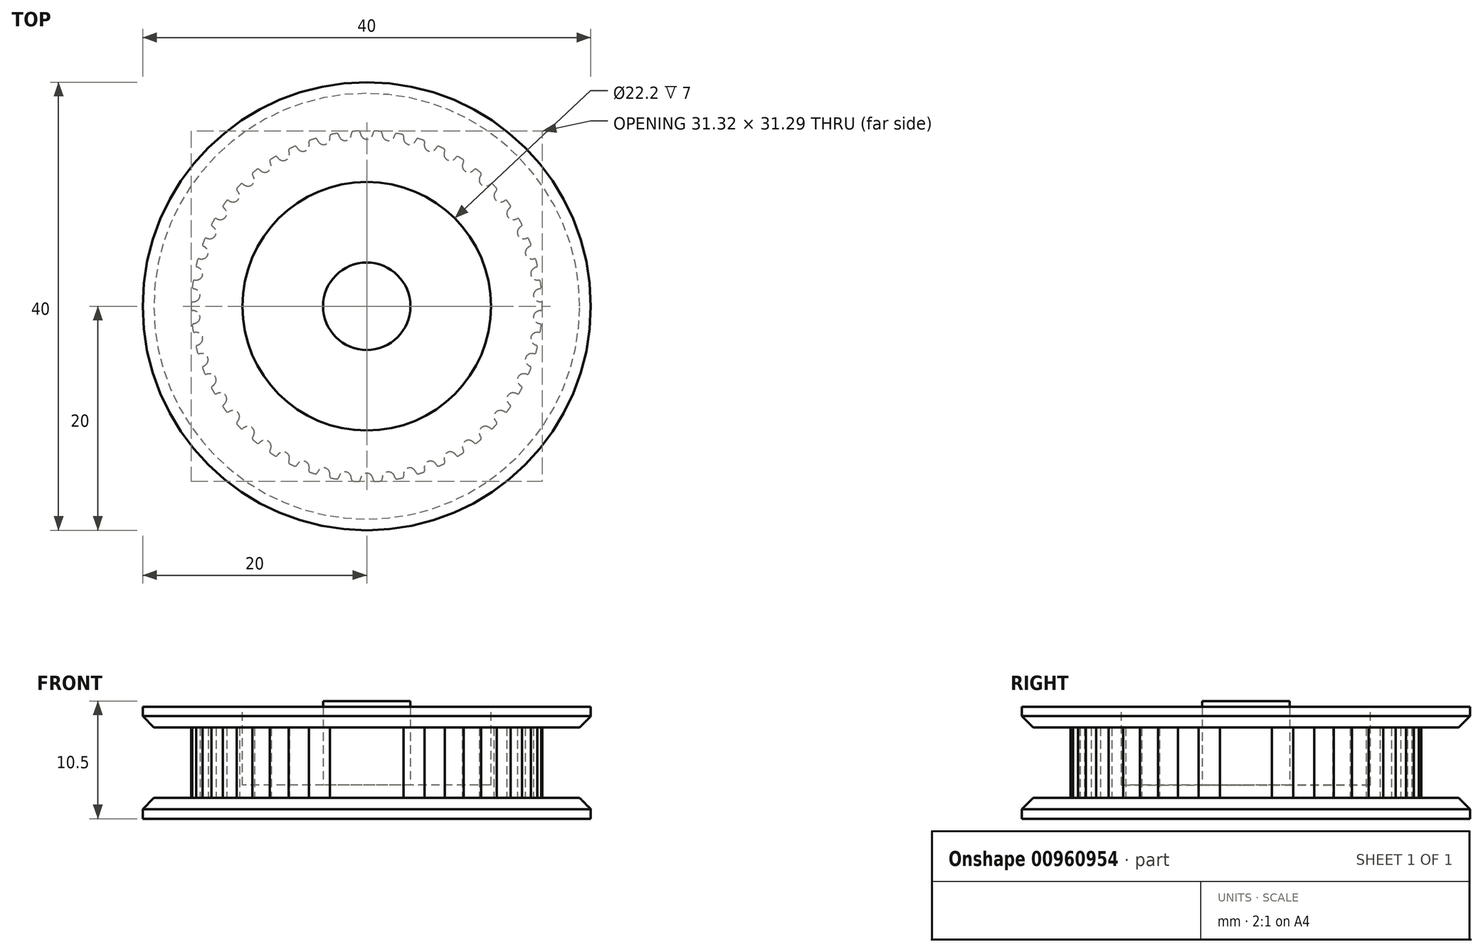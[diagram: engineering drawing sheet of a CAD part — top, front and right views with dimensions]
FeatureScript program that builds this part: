
annotation { "Feature Type Name" : "Feature", "Feature Type Description" : "" }
export const myFeature = defineFeature(function(context is Context, id is Id, definition is map)
    precondition{}
    {
        {
            assignVariable(context, id + "F0", {"variableType" : VariableType.NUMBER, "name" : "TeethP1", "numberValue" : 50});
        }
        {
            assignVariable(context, id + "F1", {"variableType" : VariableType.LENGTH, "name" : "PulleyDepth", "lengthValue" : 10 * mm});
        }
        {
            assignVariable(context, id + "F2", {"variableType" : VariableType.LENGTH, "name" : "BeltWidth", "lengthValue" : 6.3 * mm});
        }
        {
            var Q0;
            Q0=qCreatedBy(makeId("Top.planeOp"),FACE);
            var sketch = newSketch(context, id + "F3", { "sketchPlane" : qUnion([Q0])});
            skPoint(sketch, "E0.center", {"position": v(0, 0) * mm});
            skCircle(sketch, "E1", {"center": v(0, 0) * mm, "radius": 20 * mm});
            skSolve(sketch);
        }
        {
            var Q0;
            Q0 = qSketchRegion(id + "F3", true);
            extrude(context, id + "F4", {"entities" : qUnion([Q0]), "depth" : (getVariable(context, 'PulleyDepth') - getVariable(context, 'BeltWidth')) / 2, "offsetDistance" : 25 * mm});
        }
        {
            var Q0;
            Q0=makeQuery(id+"F4.opExtrude","CAP_FACE",FACE,{"disambiguationData":[OSD([sQuery(id+"F3.wireOp",EDGE,"E1")])],"isStart":false});
            var sketch = newSketch(context, id + "F5", { "sketchPlane" : qUnion([Q0])});
            skCircle(sketch, "E2", {"center": v(0, 0) * mm, "radius": 16.3 * mm, "construction": true});
            skLineSegment(sketch, "E3", {"start": v(0, 0) * mm, "end": v(0, -14.91) * mm});
            skCircle(sketch, "E4", {"center": v(0, 0) * mm, "radius": 14.91 * mm, "construction": true});
            skCircle(sketch, "E5", {"center": v(0, 0) * mm, "radius": 15.66 * mm, "construction": true});
            skCircle(sketch, "E6", {"center": v(0, 0) * mm, "radius": 15.92 * mm, "construction": true});
            skPoint(sketch, "E7", {"position": v(0, -15.92) * mm});
            skArc(sketch, "E8", {"start": v(-0.5, -15.22) * mm, "mid": v(-0.56, -15.37) * mm, "end": v(-0.59, -15.52) * mm});
            skArc(sketch, "E9", {"start": v(0, -14.91) * mm, "mid": v(-0.3, -15) * mm, "end": v(-0.5, -15.22) * mm});
            skArc(sketch, "E10", {"start": v(-0.59, -15.52) * mm, "mid": v(-0.64, -15.6) * mm, "end": v(-0.74, -15.64) * mm});
            skLineSegment(sketch, "E11", {"start": v(0, 0) * mm, "end": v(-0.98, -15.63) * mm, "construction": true});
            skArc(sketch, "E12", {"start": v(-0.74, -15.64) * mm, "mid": v(-0.86, -15.64) * mm, "end": v(-0.98, -15.63) * mm});
            skLineSegment(sketch, "E13.trimOffspring", {"start": v(0, -15.47) * mm, "end": v(0, -16.3) * mm, "construction": true});
            skLineSegment(sketch, "E14.MirrorCS", {"start": v(0, 0) * mm, "end": v(-1.87, -14.8) * mm});
            skArc(sketch, "E15.MirrorCS", {"start": v(-1.87, -14.8) * mm, "mid": v(-1.59, -14.91) * mm, "end": v(-1.41, -15.17) * mm});
            skArc(sketch, "E16.MirrorCS", {"start": v(-1.41, -15.17) * mm, "mid": v(-1.37, -15.31) * mm, "end": v(-1.36, -15.47) * mm});
            skArc(sketch, "E17.MirrorCS", {"start": v(-1.36, -15.47) * mm, "mid": v(-1.32, -15.57) * mm, "end": v(-1.22, -15.61) * mm});
            skArc(sketch, "E18.MirrorCS", {"start": v(-1.22, -15.61) * mm, "mid": v(-1.1, -15.62) * mm, "end": v(-0.98, -15.63) * mm});
            skSolve(sketch);
        }
        {
            var Q0;
            Q0=makeQuery(id+"F5.imprint","IMPRINT",FACE,{"disambiguationData":[TD([[makeQuery(id+"F5.imprint","IMPRINT",EDGE,{"derivedFrom":sQuery(id+"F5.wireOp",EDGE,"E3")}),-1.0]])]});
            extrude(context, id + "F6", {"entities" : qUnion([Q0]), "depth" : getVariable(context, 'BeltWidth'), "offsetDistance" : 25 * mm});
        }
        {
            var Q0;
            Q0=makeQuery(id+"F6.opExtrude","SWEPT_BODY",BODY,{"disambiguationData":[OSD([sQuery(id+"F5.wireOp",EDGE,"E3"),sQuery(id+"F5.wireOp",EDGE,"E8"),sQuery(id+"F5.wireOp",EDGE,"E9"),sQuery(id+"F5.wireOp",EDGE,"E10"),sQuery(id+"F5.wireOp",EDGE,"E12"),sQuery(id+"F5.wireOp",EDGE,"E14.MirrorCS"),sQuery(id+"F5.wireOp",EDGE,"E15.MirrorCS"),sQuery(id+"F5.wireOp",EDGE,"E16.MirrorCS"),sQuery(id+"F5.wireOp",EDGE,"E17.MirrorCS"),sQuery(id+"F5.wireOp",EDGE,"E18.MirrorCS")])]});
            var Q1;
            Q1=makeQuery(id+"F6.opExtrude","SWEPT_EDGE",EDGE,{"disambiguationData":[OSD([sQuery(id+"F5.wireOp",EDGE,"E3"),sQuery(id+"F5.wireOp",EDGE,"E14.MirrorCS")])]});
            circularPattern(context, id + "F7", {"operationType" : NewBodyOperationType.ADD, "entities" : qUnion([Q0]), "axis" : qUnion([Q1]), "angle" : 360 * degree, "instanceCount" : getVariable(context, 'TeethP1'), "equalSpace" : true});
        }
        {
            var Q0;
            Q0=makeQuery(id+"F4.opExtrude","CAP_FACE",FACE,{"disambiguationData":[OSD([sQuery(id+"F3.wireOp",EDGE,"E1")])],"isStart":true});
            var Q1;
            {var subQ0=makeQuery(id+"F6.opExtrude","CAP_FACE",FACE,{"disambiguationData":[OSD([sQuery(id+"F5.wireOp",EDGE,"E3"),sQuery(id+"F5.wireOp",EDGE,"E8"),sQuery(id+"F5.wireOp",EDGE,"E9"),sQuery(id+"F5.wireOp",EDGE,"E10"),sQuery(id+"F5.wireOp",EDGE,"E12"),sQuery(id+"F5.wireOp",EDGE,"E14.MirrorCS"),sQuery(id+"F5.wireOp",EDGE,"E15.MirrorCS"),sQuery(id+"F5.wireOp",EDGE,"E16.MirrorCS"),sQuery(id+"F5.wireOp",EDGE,"E17.MirrorCS"),sQuery(id+"F5.wireOp",EDGE,"E18.MirrorCS")])],"isStart":false});Q1=makeQuery(id+"F7.boolean.opBoolean","MERGE",FACE,{"derivedFrom":[subQ0,makeQuery(id+"F7.opPattern","COPY",FACE,{"derivedFrom":subQ0,"instanceName":"1"}),makeQuery(id+"F7.opPattern","COPY",FACE,{"derivedFrom":subQ0,"instanceName":"2"}),makeQuery(id+"F7.opPattern","COPY",FACE,{"derivedFrom":subQ0,"instanceName":"3"}),makeQuery(id+"F7.opPattern","COPY",FACE,{"derivedFrom":subQ0,"instanceName":"4"}),makeQuery(id+"F7.opPattern","COPY",FACE,{"derivedFrom":subQ0,"instanceName":"5"}),makeQuery(id+"F7.opPattern","COPY",FACE,{"derivedFrom":subQ0,"instanceName":"6"}),makeQuery(id+"F7.opPattern","COPY",FACE,{"derivedFrom":subQ0,"instanceName":"7"}),makeQuery(id+"F7.opPattern","COPY",FACE,{"derivedFrom":subQ0,"instanceName":"8"}),makeQuery(id+"F7.opPattern","COPY",FACE,{"derivedFrom":subQ0,"instanceName":"9"}),makeQuery(id+"F7.opPattern","COPY",FACE,{"derivedFrom":subQ0,"instanceName":"10"}),makeQuery(id+"F7.opPattern","COPY",FACE,{"derivedFrom":subQ0,"instanceName":"11"}),makeQuery(id+"F7.opPattern","COPY",FACE,{"derivedFrom":subQ0,"instanceName":"12"}),makeQuery(id+"F7.opPattern","COPY",FACE,{"derivedFrom":subQ0,"instanceName":"13"}),makeQuery(id+"F7.opPattern","COPY",FACE,{"derivedFrom":subQ0,"instanceName":"14"}),makeQuery(id+"F7.opPattern","COPY",FACE,{"derivedFrom":subQ0,"instanceName":"15"}),makeQuery(id+"F7.opPattern","COPY",FACE,{"derivedFrom":subQ0,"instanceName":"16"}),makeQuery(id+"F7.opPattern","COPY",FACE,{"derivedFrom":subQ0,"instanceName":"17"}),makeQuery(id+"F7.opPattern","COPY",FACE,{"derivedFrom":subQ0,"instanceName":"18"}),makeQuery(id+"F7.opPattern","COPY",FACE,{"derivedFrom":subQ0,"instanceName":"19"}),makeQuery(id+"F7.opPattern","COPY",FACE,{"derivedFrom":subQ0,"instanceName":"20"}),makeQuery(id+"F7.opPattern","COPY",FACE,{"derivedFrom":subQ0,"instanceName":"21"}),makeQuery(id+"F7.opPattern","COPY",FACE,{"derivedFrom":subQ0,"instanceName":"22"}),makeQuery(id+"F7.opPattern","COPY",FACE,{"derivedFrom":subQ0,"instanceName":"23"}),makeQuery(id+"F7.opPattern","COPY",FACE,{"derivedFrom":subQ0,"instanceName":"24"}),makeQuery(id+"F7.opPattern","COPY",FACE,{"derivedFrom":subQ0,"instanceName":"25"}),makeQuery(id+"F7.opPattern","COPY",FACE,{"derivedFrom":subQ0,"instanceName":"26"}),makeQuery(id+"F7.opPattern","COPY",FACE,{"derivedFrom":subQ0,"instanceName":"27"}),makeQuery(id+"F7.opPattern","COPY",FACE,{"derivedFrom":subQ0,"instanceName":"28"}),makeQuery(id+"F7.opPattern","COPY",FACE,{"derivedFrom":subQ0,"instanceName":"29"}),makeQuery(id+"F7.opPattern","COPY",FACE,{"derivedFrom":subQ0,"instanceName":"30"}),makeQuery(id+"F7.opPattern","COPY",FACE,{"derivedFrom":subQ0,"instanceName":"31"}),makeQuery(id+"F7.opPattern","COPY",FACE,{"derivedFrom":subQ0,"instanceName":"32"}),makeQuery(id+"F7.opPattern","COPY",FACE,{"derivedFrom":subQ0,"instanceName":"33"}),makeQuery(id+"F7.opPattern","COPY",FACE,{"derivedFrom":subQ0,"instanceName":"34"}),makeQuery(id+"F7.opPattern","COPY",FACE,{"derivedFrom":subQ0,"instanceName":"35"}),makeQuery(id+"F7.opPattern","COPY",FACE,{"derivedFrom":subQ0,"instanceName":"36"}),makeQuery(id+"F7.opPattern","COPY",FACE,{"derivedFrom":subQ0,"instanceName":"37"}),makeQuery(id+"F7.opPattern","COPY",FACE,{"derivedFrom":subQ0,"instanceName":"38"}),makeQuery(id+"F7.opPattern","COPY",FACE,{"derivedFrom":subQ0,"instanceName":"39"}),makeQuery(id+"F7.opPattern","COPY",FACE,{"derivedFrom":subQ0,"instanceName":"40"}),makeQuery(id+"F7.opPattern","COPY",FACE,{"derivedFrom":subQ0,"instanceName":"41"}),makeQuery(id+"F7.opPattern","COPY",FACE,{"derivedFrom":subQ0,"instanceName":"42"}),makeQuery(id+"F7.opPattern","COPY",FACE,{"derivedFrom":subQ0,"instanceName":"43"}),makeQuery(id+"F7.opPattern","COPY",FACE,{"derivedFrom":subQ0,"instanceName":"44"}),makeQuery(id+"F7.opPattern","COPY",FACE,{"derivedFrom":subQ0,"instanceName":"45"}),makeQuery(id+"F7.opPattern","COPY",FACE,{"derivedFrom":subQ0,"instanceName":"46"}),makeQuery(id+"F7.opPattern","COPY",FACE,{"derivedFrom":subQ0,"instanceName":"47"}),makeQuery(id+"F7.opPattern","COPY",FACE,{"derivedFrom":subQ0,"instanceName":"48"}),makeQuery(id+"F7.opPattern","COPY",FACE,{"derivedFrom":subQ0,"instanceName":"49"}),makeQuery(id+"F7.opPattern","COPY",FACE,{"derivedFrom":subQ0,"instanceName":"50"}),makeQuery(id+"F7.opPattern","COPY",FACE,{"derivedFrom":subQ0,"instanceName":"51"}),makeQuery(id+"F7.opPattern","COPY",FACE,{"derivedFrom":subQ0,"instanceName":"52"}),makeQuery(id+"F7.opPattern","COPY",FACE,{"derivedFrom":subQ0,"instanceName":"53"}),makeQuery(id+"F7.opPattern","COPY",FACE,{"derivedFrom":subQ0,"instanceName":"54"}),makeQuery(id+"F7.opPattern","COPY",FACE,{"derivedFrom":subQ0,"instanceName":"55"}),makeQuery(id+"F7.opPattern","COPY",FACE,{"derivedFrom":subQ0,"instanceName":"56"}),makeQuery(id+"F7.opPattern","COPY",FACE,{"derivedFrom":subQ0,"instanceName":"57"}),makeQuery(id+"F7.opPattern","COPY",FACE,{"derivedFrom":subQ0,"instanceName":"58"}),makeQuery(id+"F7.opPattern","COPY",FACE,{"derivedFrom":subQ0,"instanceName":"59"})]});}
            var Q2;
            {var subQ0=makeQuery(id+"F6.opExtrude","CAP_FACE",FACE,{"disambiguationData":[OSD([sQuery(id+"F5.wireOp",EDGE,"E3"),sQuery(id+"F5.wireOp",EDGE,"E8"),sQuery(id+"F5.wireOp",EDGE,"E9"),sQuery(id+"F5.wireOp",EDGE,"E10"),sQuery(id+"F5.wireOp",EDGE,"E12"),sQuery(id+"F5.wireOp",EDGE,"E14.MirrorCS"),sQuery(id+"F5.wireOp",EDGE,"E15.MirrorCS"),sQuery(id+"F5.wireOp",EDGE,"E16.MirrorCS"),sQuery(id+"F5.wireOp",EDGE,"E17.MirrorCS"),sQuery(id+"F5.wireOp",EDGE,"E18.MirrorCS")])],"isStart":false});Q2=makeQuery(id+"F7.boolean.opBoolean","MERGE",FACE,{"derivedFrom":[subQ0,makeQuery(id+"F7.opPattern","COPY",FACE,{"derivedFrom":subQ0,"instanceName":"1"}),makeQuery(id+"F7.opPattern","COPY",FACE,{"derivedFrom":subQ0,"instanceName":"2"}),makeQuery(id+"F7.opPattern","COPY",FACE,{"derivedFrom":subQ0,"instanceName":"3"}),makeQuery(id+"F7.opPattern","COPY",FACE,{"derivedFrom":subQ0,"instanceName":"4"}),makeQuery(id+"F7.opPattern","COPY",FACE,{"derivedFrom":subQ0,"instanceName":"5"}),makeQuery(id+"F7.opPattern","COPY",FACE,{"derivedFrom":subQ0,"instanceName":"6"}),makeQuery(id+"F7.opPattern","COPY",FACE,{"derivedFrom":subQ0,"instanceName":"7"}),makeQuery(id+"F7.opPattern","COPY",FACE,{"derivedFrom":subQ0,"instanceName":"8"}),makeQuery(id+"F7.opPattern","COPY",FACE,{"derivedFrom":subQ0,"instanceName":"9"}),makeQuery(id+"F7.opPattern","COPY",FACE,{"derivedFrom":subQ0,"instanceName":"10"}),makeQuery(id+"F7.opPattern","COPY",FACE,{"derivedFrom":subQ0,"instanceName":"11"}),makeQuery(id+"F7.opPattern","COPY",FACE,{"derivedFrom":subQ0,"instanceName":"12"}),makeQuery(id+"F7.opPattern","COPY",FACE,{"derivedFrom":subQ0,"instanceName":"13"}),makeQuery(id+"F7.opPattern","COPY",FACE,{"derivedFrom":subQ0,"instanceName":"14"}),makeQuery(id+"F7.opPattern","COPY",FACE,{"derivedFrom":subQ0,"instanceName":"15"}),makeQuery(id+"F7.opPattern","COPY",FACE,{"derivedFrom":subQ0,"instanceName":"16"}),makeQuery(id+"F7.opPattern","COPY",FACE,{"derivedFrom":subQ0,"instanceName":"17"}),makeQuery(id+"F7.opPattern","COPY",FACE,{"derivedFrom":subQ0,"instanceName":"18"}),makeQuery(id+"F7.opPattern","COPY",FACE,{"derivedFrom":subQ0,"instanceName":"19"}),makeQuery(id+"F7.opPattern","COPY",FACE,{"derivedFrom":subQ0,"instanceName":"20"}),makeQuery(id+"F7.opPattern","COPY",FACE,{"derivedFrom":subQ0,"instanceName":"21"}),makeQuery(id+"F7.opPattern","COPY",FACE,{"derivedFrom":subQ0,"instanceName":"22"}),makeQuery(id+"F7.opPattern","COPY",FACE,{"derivedFrom":subQ0,"instanceName":"23"}),makeQuery(id+"F7.opPattern","COPY",FACE,{"derivedFrom":subQ0,"instanceName":"24"}),makeQuery(id+"F7.opPattern","COPY",FACE,{"derivedFrom":subQ0,"instanceName":"25"}),makeQuery(id+"F7.opPattern","COPY",FACE,{"derivedFrom":subQ0,"instanceName":"26"}),makeQuery(id+"F7.opPattern","COPY",FACE,{"derivedFrom":subQ0,"instanceName":"27"}),makeQuery(id+"F7.opPattern","COPY",FACE,{"derivedFrom":subQ0,"instanceName":"28"}),makeQuery(id+"F7.opPattern","COPY",FACE,{"derivedFrom":subQ0,"instanceName":"29"}),makeQuery(id+"F7.opPattern","COPY",FACE,{"derivedFrom":subQ0,"instanceName":"30"}),makeQuery(id+"F7.opPattern","COPY",FACE,{"derivedFrom":subQ0,"instanceName":"31"}),makeQuery(id+"F7.opPattern","COPY",FACE,{"derivedFrom":subQ0,"instanceName":"32"}),makeQuery(id+"F7.opPattern","COPY",FACE,{"derivedFrom":subQ0,"instanceName":"33"}),makeQuery(id+"F7.opPattern","COPY",FACE,{"derivedFrom":subQ0,"instanceName":"34"}),makeQuery(id+"F7.opPattern","COPY",FACE,{"derivedFrom":subQ0,"instanceName":"35"}),makeQuery(id+"F7.opPattern","COPY",FACE,{"derivedFrom":subQ0,"instanceName":"36"}),makeQuery(id+"F7.opPattern","COPY",FACE,{"derivedFrom":subQ0,"instanceName":"37"}),makeQuery(id+"F7.opPattern","COPY",FACE,{"derivedFrom":subQ0,"instanceName":"38"}),makeQuery(id+"F7.opPattern","COPY",FACE,{"derivedFrom":subQ0,"instanceName":"39"}),makeQuery(id+"F7.opPattern","COPY",FACE,{"derivedFrom":subQ0,"instanceName":"40"}),makeQuery(id+"F7.opPattern","COPY",FACE,{"derivedFrom":subQ0,"instanceName":"41"}),makeQuery(id+"F7.opPattern","COPY",FACE,{"derivedFrom":subQ0,"instanceName":"42"}),makeQuery(id+"F7.opPattern","COPY",FACE,{"derivedFrom":subQ0,"instanceName":"43"}),makeQuery(id+"F7.opPattern","COPY",FACE,{"derivedFrom":subQ0,"instanceName":"44"}),makeQuery(id+"F7.opPattern","COPY",FACE,{"derivedFrom":subQ0,"instanceName":"45"}),makeQuery(id+"F7.opPattern","COPY",FACE,{"derivedFrom":subQ0,"instanceName":"46"}),makeQuery(id+"F7.opPattern","COPY",FACE,{"derivedFrom":subQ0,"instanceName":"47"}),makeQuery(id+"F7.opPattern","COPY",FACE,{"derivedFrom":subQ0,"instanceName":"48"}),makeQuery(id+"F7.opPattern","COPY",FACE,{"derivedFrom":subQ0,"instanceName":"49"}),makeQuery(id+"F7.opPattern","COPY",FACE,{"derivedFrom":subQ0,"instanceName":"50"}),makeQuery(id+"F7.opPattern","COPY",FACE,{"derivedFrom":subQ0,"instanceName":"51"}),makeQuery(id+"F7.opPattern","COPY",FACE,{"derivedFrom":subQ0,"instanceName":"52"}),makeQuery(id+"F7.opPattern","COPY",FACE,{"derivedFrom":subQ0,"instanceName":"53"}),makeQuery(id+"F7.opPattern","COPY",FACE,{"derivedFrom":subQ0,"instanceName":"54"}),makeQuery(id+"F7.opPattern","COPY",FACE,{"derivedFrom":subQ0,"instanceName":"55"}),makeQuery(id+"F7.opPattern","COPY",FACE,{"derivedFrom":subQ0,"instanceName":"56"}),makeQuery(id+"F7.opPattern","COPY",FACE,{"derivedFrom":subQ0,"instanceName":"57"}),makeQuery(id+"F7.opPattern","COPY",FACE,{"derivedFrom":subQ0,"instanceName":"58"}),makeQuery(id+"F7.opPattern","COPY",FACE,{"derivedFrom":subQ0,"instanceName":"59"})]});}
            extrude(context, id + "F8", {"entities" : qUnion([Q0]), "operationType" : NewBodyOperationType.ADD, "endBound" : BoundingType.UP_TO_SURFACE, "oppositeDirection" : true, "depth" : 25 * mm, "endBoundEntityFace" : qUnion([Q1]), "hasOffset" : true, "offsetDistance" : (getVariable(context, 'PulleyDepth') - getVariable(context, 'BeltWidth')) / 2, "offsetOppositeDirection" : true, "hasSecondDirection" : true, "secondDirectionBound" : SecondDirectionBoundingType.UP_TO_SURFACE, "secondDirectionOppositeDirection" : true, "secondDirectionDepth" : 25 * mm, "secondDirectionBoundEntityFace" : qUnion([Q2])});
        }
        {
            var Q0;
            Q0=makeQuery(id+"F8.opExtrude","CAP_FACE",FACE,{"disambiguationData":[OSD([sQuery(id+"F3.wireOp",EDGE,"E1")])],"isStart":false});
            var sketch = newSketch(context, id + "F9", { "sketchPlane" : qUnion([Q0])});
            skCircle(sketch, "E19", {"center": v(0, 0) * mm, "radius": 11 * mm, "construction": true});
            skCircle(sketch, "E20", {"center": v(0, 0) * mm, "radius": 4 * mm, "construction": true});
            skCircle(sketch, "E21.0", {"center": v(0, 0) * mm, "radius": 11.1 * mm});
            skCircle(sketch, "E22.0", {"center": v(0, 0) * mm, "radius": 10.9 * mm});
            skCircle(sketch, "E23.0", {"center": v(0, 0) * mm, "radius": 3.9 * mm});
            skCircle(sketch, "E24", {"center": v(0, 0) * mm, "radius": 6 * mm});
            skSolve(sketch);
        }
        {
            var Q0;
            Q0=qSketchRegion(id+"F9",true);
            var Q1;
            Q1=makeQuery(id+"F9.imprint","IMPRINT",FACE,{"disambiguationData":[TD([[makeQuery(id+"F9.imprint","IMPRINT",EDGE,{"derivedFrom":sQuery(id+"F9.wireOp",EDGE,"E22.0")}),1.0]])]});
            var Q2;
            Q2=makeQuery(id+"F9.imprint","IMPRINT",FACE,{"disambiguationData":[TD([[makeQuery(id+"F9.imprint","IMPRINT",EDGE,{"derivedFrom":sQuery(id+"F9.wireOp",EDGE,"E23.0")}),1.0]])]});
            var Q3;
            Q3=makeQuery(id+"F9.imprint","IMPRINT",FACE,{"disambiguationData":[TD([[makeQuery(id+"F9.imprint","IMPRINT",EDGE,{"derivedFrom":sQuery(id+"F9.wireOp",EDGE,"E23.0")}),-1.0]])]});
            extrude(context, id + "F10", {"entities" : qUnion([Q0, Q1, Q2, Q3]), "operationType" : NewBodyOperationType.REMOVE, "oppositeDirection" : true, "depth" : 7 * mm, "offsetDistance" : 25 * mm});
        }
        {
            var Q0;
            Q0=makeQuery(id+"F9.imprint","IMPRINT",FACE,{"disambiguationData":[TD([[makeQuery(id+"F9.imprint","IMPRINT",EDGE,{"derivedFrom":sQuery(id+"F9.wireOp",EDGE,"E23.0")}),1.0]])]});
            extrude(context, id + "F11", {"entities" : qUnion([Q0]), "depth" : 0.5 * mm, "offsetDistance" : 25 * mm, "hasSecondDirection" : true, "secondDirectionBound" : SecondDirectionBoundingType.UP_TO_NEXT, "secondDirectionOppositeDirection" : true, "secondDirectionDepth" : 25 * mm});
        }
        {
            var Q0;
            Q0=makeQuery(id+"F8.opExtrude","CAP_EDGE",EDGE,{"disambiguationData":[OSD([sQuery(id+"F3.wireOp",EDGE,"E1")])],"isStart":true});
            var Q1;
            Q1=makeQuery(id+"F4.opExtrude","CAP_EDGE",EDGE,{"disambiguationData":[OSD([sQuery(id+"F3.wireOp",EDGE,"E1")])],"isStart":false});
            chamfer(context, id + "F12", {"entities" : qUnion([Q0, Q1]), "width" : 1 * mm, "tangentPropagation" : true});
        }
    });
